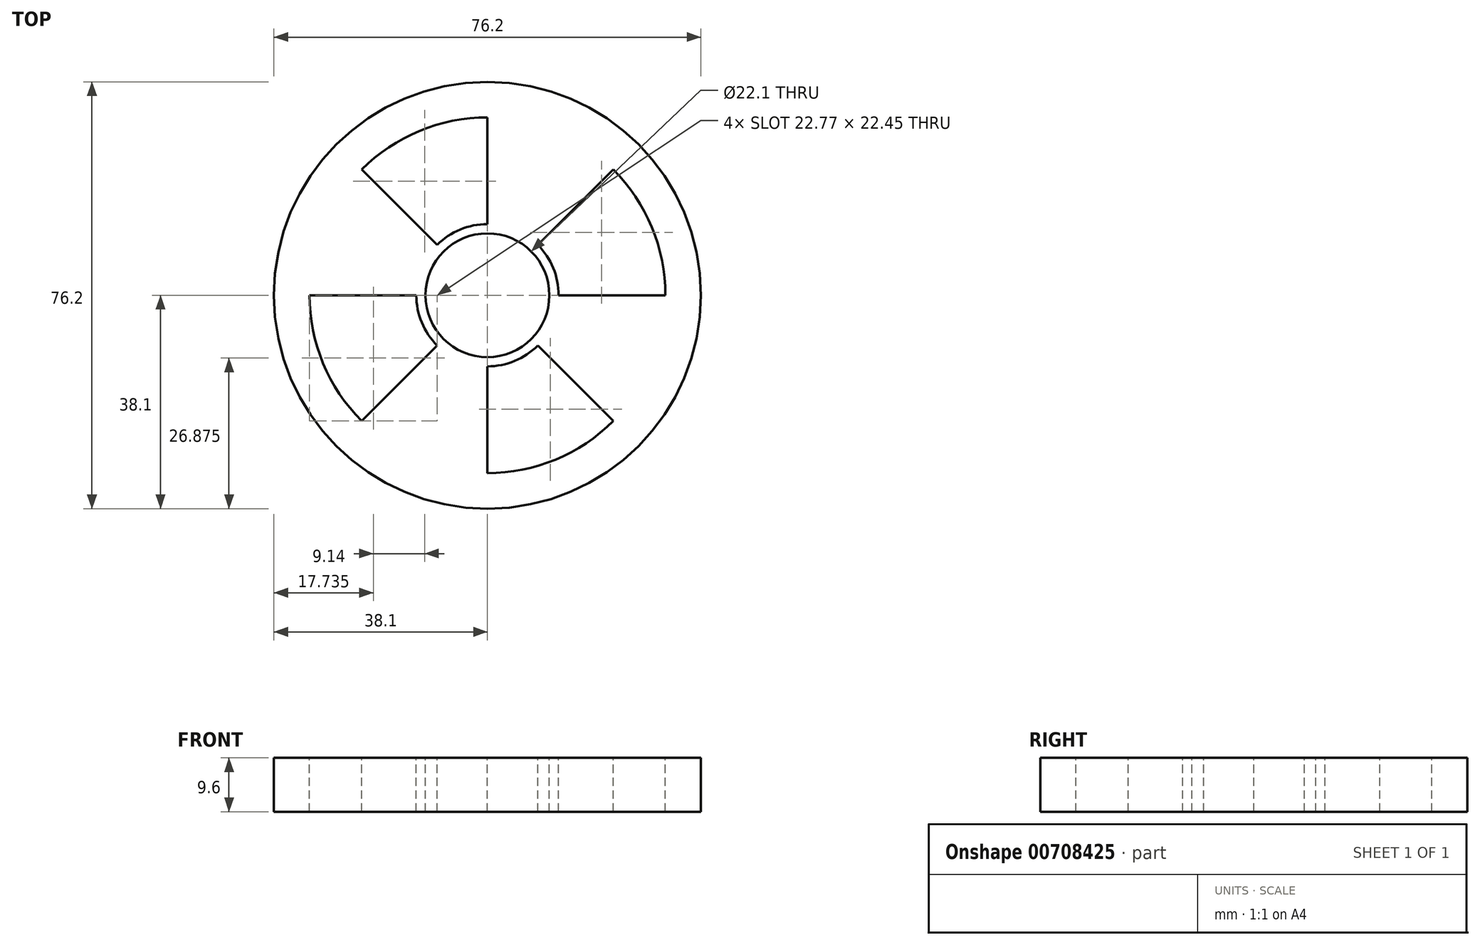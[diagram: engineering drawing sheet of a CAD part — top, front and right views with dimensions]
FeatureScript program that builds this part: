
annotation { "Feature Type Name" : "Feature", "Feature Type Description" : "" }
export const myFeature = defineFeature(function(context is Context, id is Id, definition is map)
    precondition{}
    {
        {
            var Q0;
            Q0=qCreatedBy(makeId("Top.planeOp"),FACE);
            var sketch = newSketch(context, id + "F0", { "sketchPlane" : qUnion([Q0])});
            skCircle(sketch, "E0", {"center": v(0, 0) * mm, "radius": 38.1 * mm});
            skSolve(sketch);
        }
        {
            var Q0;
            Q0 = qSketchRegion(id + "F0", true);
            extrude(context, id + "F1", {"entities" : qUnion([Q0]), "endBound" : BoundingType.SYMMETRIC, "depth" : 9.6 * mm, "offsetDistance" : 25.4 * mm});
        }
        {
            var Q0;
            Q0=makeQuery(id+"F1.opExtrude","CAP_FACE",FACE,{"disambiguationData":[OSD([sQuery(id+"F0.wireOp",EDGE,"E0")])],"isStart":false});
            var sketch = newSketch(context, id + "F2", { "sketchPlane" : qUnion([Q0])});
            skCircle(sketch, "E1", {"center": v(0, 0) * mm, "radius": 12.7 * mm});
            skCircle(sketch, "E2", {"center": v(0, 0) * mm, "radius": 25.4 * mm});
            skCircle(sketch, "E3", {"center": v(0, 0) * mm, "radius": 19.05 * mm});
            skCircle(sketch, "E4", {"center": v(0, 0) * mm, "radius": 31.75 * mm});
            skLineSegment(sketch, "E5", {"start": v(0, 12.7) * mm, "end": v(0, 31.75) * mm});
            skLineSegment(sketch, "E6.1.0", {"start": v(-8.98, 8.98) * mm, "end": v(-22.45, 22.45) * mm});
            skLineSegment(sketch, "E6.2.0", {"start": v(-12.7, 0) * mm, "end": v(-31.75, 0) * mm});
            skLineSegment(sketch, "E6.3.0", {"start": v(-8.98, -8.98) * mm, "end": v(-22.45, -22.45) * mm});
            skLineSegment(sketch, "E6.4.0", {"start": v(0, -12.7) * mm, "end": v(0, -31.75) * mm});
            skLineSegment(sketch, "E6.5.0", {"start": v(8.98, -8.98) * mm, "end": v(22.45, -22.45) * mm});
            skLineSegment(sketch, "E6.6.0", {"start": v(12.7, 0) * mm, "end": v(31.75, 0) * mm});
            skLineSegment(sketch, "E6.7.0", {"start": v(8.98, 8.98) * mm, "end": v(22.45, 22.45) * mm});
            skSolve(sketch);
        }
        {
            var Q0;
            Q0=makeQuery(id+"F1.opExtrude","CAP_FACE",FACE,{"disambiguationData":[OSD([sQuery(id+"F0.wireOp",EDGE,"E0")])],"isStart":false});
            var sketch = newSketch(context, id + "F3", { "sketchPlane" : qUnion([Q0])});
            skCircle(sketch, "E7", {"center": v(0, 0) * mm, "radius": 11.05 * mm});
            skSolve(sketch);
        }
        {
            var Q0;
            Q0 = qSketchRegion(id + "F3", true);
            extrude(context, id + "F4", {"entities" : qUnion([Q0]), "operationType" : NewBodyOperationType.REMOVE, "oppositeDirection" : true, "depth" : 25.4 * mm, "offsetDistance" : 25.4 * mm});
        }
        {
            var Q0;
            {var subQ0=sQuery(id+"F2.wireOp",EDGE,"E6.7.0");var subQ1=sQuery(id+"F2.wireOp",EDGE,"E2");var subQ2=makeQuery(id+"F2.imprint","INTERSECT",VERTEX,{"derivedFrom":[subQ1,subQ0]});Q0=makeQuery(id+"F2.imprint","IMPRINT",FACE,{"disambiguationData":[TD([[makeQuery(id+"F2.imprint","IMPRINT",EDGE,{"disambiguationData":[TD([[subQ2,1.0]])],"derivedFrom":subQ1}),-1.0]])]});}
            var Q1;
            {var subQ0=sQuery(id+"F2.wireOp",EDGE,"E5");var subQ1=sQuery(id+"F2.wireOp",EDGE,"E2");var subQ2=makeQuery(id+"F2.imprint","INTERSECT",VERTEX,{"derivedFrom":[subQ1,subQ0]});Q1=makeQuery(id+"F2.imprint","IMPRINT",FACE,{"disambiguationData":[TD([[makeQuery(id+"F2.imprint","IMPRINT",EDGE,{"disambiguationData":[TD([[subQ2,-1.0]])],"derivedFrom":subQ1}),-1.0]])]});}
            var Q2;
            {var subQ0=sQuery(id+"F2.wireOp",EDGE,"E6.2.0");var subQ1=sQuery(id+"F2.wireOp",EDGE,"E2");var subQ2=makeQuery(id+"F2.imprint","INTERSECT",VERTEX,{"derivedFrom":[subQ1,subQ0]});Q2=makeQuery(id+"F2.imprint","IMPRINT",FACE,{"disambiguationData":[TD([[makeQuery(id+"F2.imprint","IMPRINT",EDGE,{"disambiguationData":[TD([[subQ2,-1.0]])],"derivedFrom":subQ1}),-1.0]])]});}
            var Q3;
            {var subQ0=sQuery(id+"F2.wireOp",EDGE,"E6.4.0");var subQ1=sQuery(id+"F2.wireOp",EDGE,"E2");var subQ2=makeQuery(id+"F2.imprint","INTERSECT",VERTEX,{"derivedFrom":[subQ1,subQ0]});Q3=makeQuery(id+"F2.imprint","IMPRINT",FACE,{"disambiguationData":[TD([[makeQuery(id+"F2.imprint","IMPRINT",EDGE,{"disambiguationData":[TD([[subQ2,-1.0]])],"derivedFrom":subQ1}),-1.0]])]});}
            var Q4;
            {var subQ0=sQuery(id+"F2.wireOp",EDGE,"E6.2.0");var subQ1=sQuery(id+"F2.wireOp",EDGE,"E1");var subQ2=makeQuery(id+"F2.imprint","INTERSECT",VERTEX,{"derivedFrom":[subQ1,subQ0]});Q4=makeQuery(id+"F2.imprint","IMPRINT",FACE,{"disambiguationData":[TD([[makeQuery(id+"F2.imprint","IMPRINT",EDGE,{"disambiguationData":[TD([[subQ2,-1.0]])],"derivedFrom":subQ1}),-1.0]])]});}
            var Q5;
            {var subQ0=sQuery(id+"F2.wireOp",EDGE,"E5");var subQ1=sQuery(id+"F2.wireOp",EDGE,"E1");var subQ2=makeQuery(id+"F2.imprint","INTERSECT",VERTEX,{"derivedFrom":[subQ1,subQ0]});Q5=makeQuery(id+"F2.imprint","IMPRINT",FACE,{"disambiguationData":[TD([[makeQuery(id+"F2.imprint","IMPRINT",EDGE,{"disambiguationData":[TD([[subQ2,-1.0]])],"derivedFrom":subQ1}),-1.0]])]});}
            var Q6;
            {var subQ0=sQuery(id+"F2.wireOp",EDGE,"E6.6.0");var subQ1=sQuery(id+"F2.wireOp",EDGE,"E1");var subQ2=makeQuery(id+"F2.imprint","INTERSECT",VERTEX,{"derivedFrom":[subQ1,subQ0]});Q6=makeQuery(id+"F2.imprint","IMPRINT",FACE,{"disambiguationData":[TD([[makeQuery(id+"F2.imprint","IMPRINT",EDGE,{"disambiguationData":[TD([[subQ2,-1.0]])],"derivedFrom":subQ1}),-1.0]])]});}
            var Q7;
            {var subQ0=sQuery(id+"F2.wireOp",EDGE,"E6.4.0");var subQ1=sQuery(id+"F2.wireOp",EDGE,"E1");var subQ2=makeQuery(id+"F2.imprint","INTERSECT",VERTEX,{"derivedFrom":[subQ1,subQ0]});Q7=makeQuery(id+"F2.imprint","IMPRINT",FACE,{"disambiguationData":[TD([[makeQuery(id+"F2.imprint","IMPRINT",EDGE,{"disambiguationData":[TD([[subQ2,-1.0]])],"derivedFrom":subQ1}),-1.0]])]});}
            var Q8;
            {var subQ0=sQuery(id+"F2.wireOp",EDGE,"E5");var subQ1=sQuery(id+"F2.wireOp",EDGE,"E2");var subQ2=makeQuery(id+"F2.imprint","INTERSECT",VERTEX,{"derivedFrom":[subQ1,subQ0]});Q8=makeQuery(id+"F2.imprint","IMPRINT",FACE,{"disambiguationData":[TD([[makeQuery(id+"F2.imprint","IMPRINT",EDGE,{"disambiguationData":[TD([[subQ2,-1.0]])],"derivedFrom":subQ1}),1.0]])]});}
            var Q9;
            {var subQ0=sQuery(id+"F2.wireOp",EDGE,"E6.7.0");var subQ1=sQuery(id+"F2.wireOp",EDGE,"E2");var subQ2=makeQuery(id+"F2.imprint","INTERSECT",VERTEX,{"derivedFrom":[subQ1,subQ0]});Q9=makeQuery(id+"F2.imprint","IMPRINT",FACE,{"disambiguationData":[TD([[makeQuery(id+"F2.imprint","IMPRINT",EDGE,{"disambiguationData":[TD([[subQ2,1.0]])],"derivedFrom":subQ1}),1.0]])]});}
            var Q10;
            {var subQ0=sQuery(id+"F2.wireOp",EDGE,"E6.2.0");var subQ1=sQuery(id+"F2.wireOp",EDGE,"E2");var subQ2=makeQuery(id+"F2.imprint","INTERSECT",VERTEX,{"derivedFrom":[subQ1,subQ0]});Q10=makeQuery(id+"F2.imprint","IMPRINT",FACE,{"disambiguationData":[TD([[makeQuery(id+"F2.imprint","IMPRINT",EDGE,{"disambiguationData":[TD([[subQ2,-1.0]])],"derivedFrom":subQ1}),1.0]])]});}
            var Q11;
            {var subQ0=sQuery(id+"F2.wireOp",EDGE,"E6.4.0");var subQ1=sQuery(id+"F2.wireOp",EDGE,"E2");var subQ2=makeQuery(id+"F2.imprint","INTERSECT",VERTEX,{"derivedFrom":[subQ1,subQ0]});Q11=makeQuery(id+"F2.imprint","IMPRINT",FACE,{"disambiguationData":[TD([[makeQuery(id+"F2.imprint","IMPRINT",EDGE,{"disambiguationData":[TD([[subQ2,-1.0]])],"derivedFrom":subQ1}),1.0]])]});}
            extrude(context, id + "F5", {"entities" : qUnion([Q0, Q1, Q2, Q3, Q4, Q5, Q6, Q7, Q8, Q9, Q10, Q11]), "operationType" : NewBodyOperationType.REMOVE, "oppositeDirection" : true, "depth" : 25.4 * mm, "offsetDistance" : 25.4 * mm});
        }
    });
